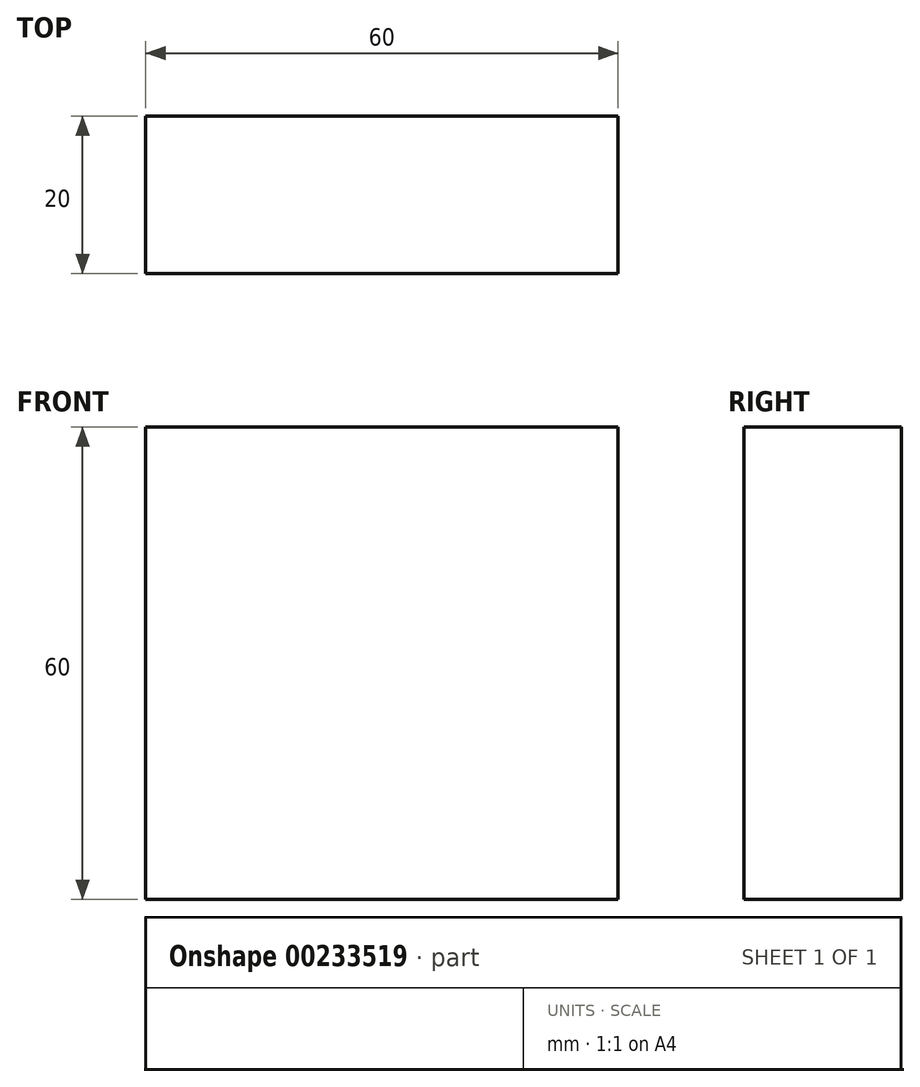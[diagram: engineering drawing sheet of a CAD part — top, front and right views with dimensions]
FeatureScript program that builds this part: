
annotation { "Feature Type Name" : "Feature", "Feature Type Description" : "" }
export const myFeature = defineFeature(function(context is Context, id is Id, definition is map)
    precondition{}
    {
        {
            var Q0;
            Q0=qCreatedBy(makeId("Front.planeOp"),FACE);
            var sketch = newSketch(context, id + "F0", { "sketchPlane" : qUnion([Q0])});
            skLineSegment(sketch, "E0.bottom", {"start": v(0, 0) * mm, "end": v(60, 0) * mm});
            skLineSegment(sketch, "E0.top", {"start": v(0, 60) * mm, "end": v(60, 60) * mm});
            skLineSegment(sketch, "E0.left", {"start": v(0, 0) * mm, "end": v(0, 60) * mm});
            skLineSegment(sketch, "E0.right", {"start": v(60, 0) * mm, "end": v(60, 60) * mm});
            skSolve(sketch);
        }
        {
            var Q0;
            Q0 = qSketchRegion(id + "F0", true);
            extrude(context, id + "F1", {"entities" : qUnion([Q0]), "depth" : 20 * mm});
        }
    });
